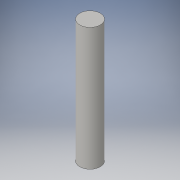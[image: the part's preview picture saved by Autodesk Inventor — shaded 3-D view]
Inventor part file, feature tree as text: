
AUTODESK INVENTOR PART (.ipt)
format: ipt  version: 2016 (Build 200138000, 138)  size: 84,992 bytes
history: native  units: in
note: dims shown in document units (in); Inventor stores cm internally (conversion verified against a paired STEP export)
features: extrude x1, sketch x1
ambient origin geometry x8: Origin, YZ Plane, XZ Plane, XY Plane, X Axis, Y Axis, Z Axis, Center Point
bodies: Solid1 (feature_tree)
feature tree (2):
  extrude  "Extrusion1"  Depth=3.0in TaperAngle=0.0deg
  sketch  "Sketch1"  dims[d0=0.5in d1=3.0in d2=0.0in]
